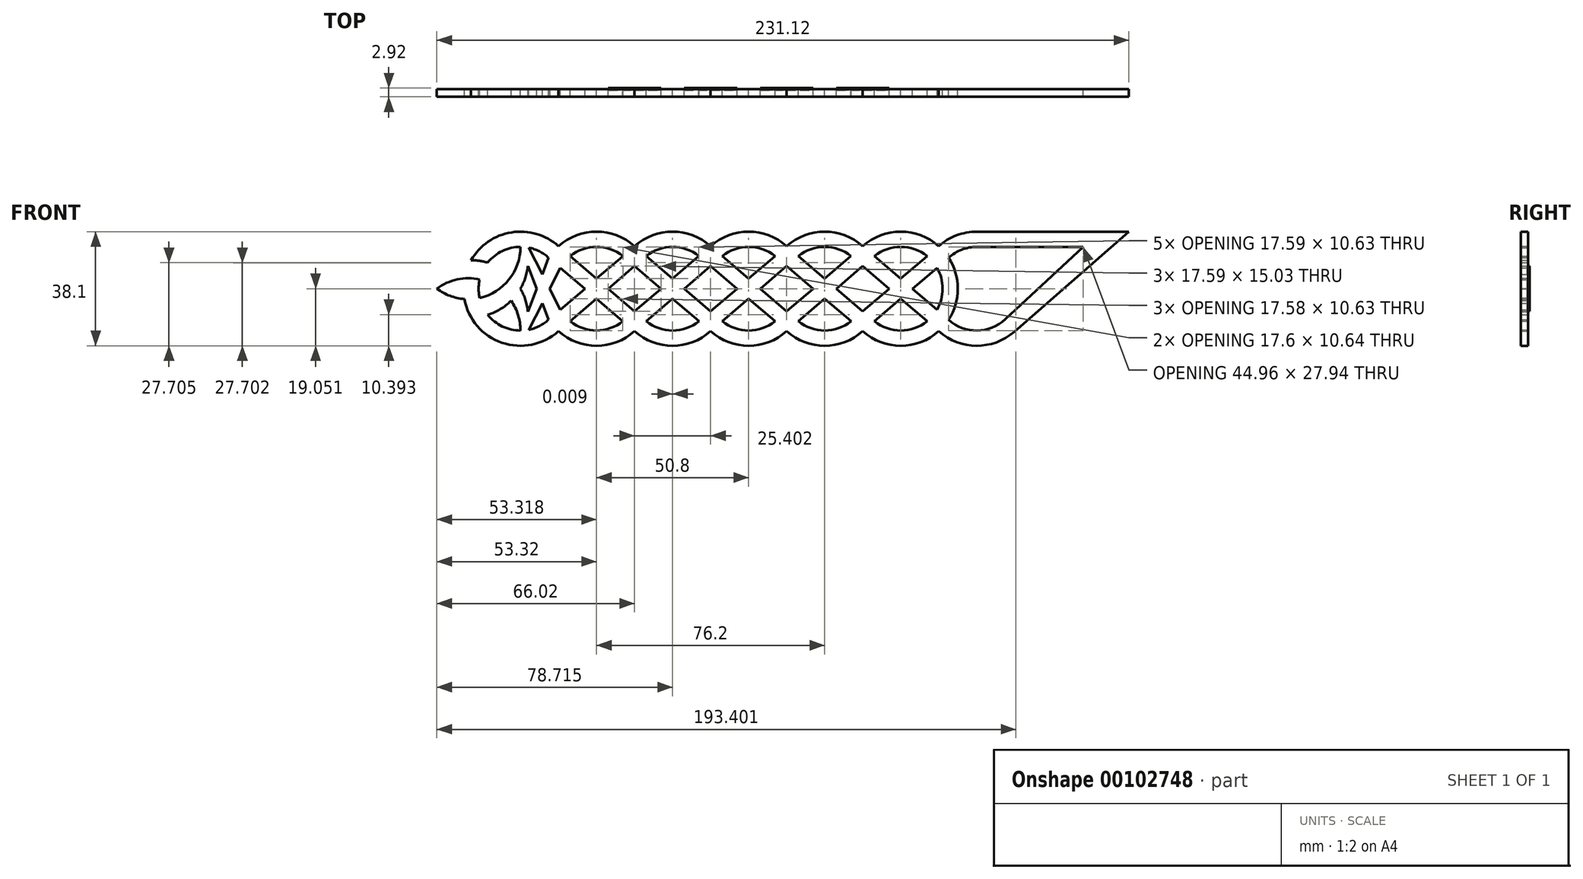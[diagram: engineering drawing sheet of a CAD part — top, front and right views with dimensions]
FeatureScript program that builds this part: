
annotation { "Feature Type Name" : "Feature", "Feature Type Description" : "" }
export const myFeature = defineFeature(function(context is Context, id is Id, definition is map)
    precondition{}
    {
        {
            var Q0;
            Q0=qCreatedBy(makeId("Front.planeOp"),FACE);
            var sketch = newSketch(context, id + "F3", { "sketchPlane" : qUnion([Q0])});
            skPoint(sketch, "E0", {"position": v(0, 0) * mm});
            skLineSegment(sketch, "E1.bottom", {"start": v(0, 0) * mm, "end": v(0, 0) * mm});
            skLineSegment(sketch, "E1.top", {"start": v(0, 0) * mm, "end": v(0, 0) * mm});
            skLineSegment(sketch, "E1.left", {"start": v(0, 0) * mm, "end": v(0, 0) * mm});
            skLineSegment(sketch, "E1.right", {"start": v(0, 0) * mm, "end": v(0, 0) * mm});
            skLineSegment(sketch, "E2.bottom", {"start": v(76.2, 19.05) * mm, "end": v(-76.2, 19.05) * mm, "construction": true});
            skLineSegment(sketch, "E2.top", {"start": v(76.2, -19.05) * mm, "end": v(-76.2, -19.05) * mm, "construction": true});
            skPoint(sketch, "E3", {"position": v(-76.2, 19.05) * mm});
            skPoint(sketch, "E4", {"position": v(76.2, 19.05) * mm});
            skPoint(sketch, "E5", {"position": v(76.2, -19.05) * mm});
            skPoint(sketch, "E6", {"position": v(-76.2, -19.05) * mm});
            skPoint(sketch, "E7", {"position": v(-76.2, 13.97) * mm});
            skPoint(sketch, "E8", {"position": v(-76.2, -13.97) * mm});
            skPoint(sketch, "E9", {"position": v(76.2, -13.97) * mm});
            skPoint(sketch, "E10", {"position": v(-50.8, 19.05) * mm});
            skPoint(sketch, "E11", {"position": v(-25.4, 19.05) * mm});
            skPoint(sketch, "E12", {"position": v(0, 19.05) * mm});
            skPoint(sketch, "E13", {"position": v(25.4, 19.05) * mm});
            skPoint(sketch, "E14", {"position": v(50.8, 19.05) * mm});
            skPoint(sketch, "E15", {"position": v(-50.8, 13.97) * mm});
            skPoint(sketch, "E16", {"position": v(-25.4, 13.97) * mm});
            skPoint(sketch, "E17", {"position": v(0, 13.97) * mm});
            skPoint(sketch, "E18", {"position": v(25.4, 13.97) * mm});
            skPoint(sketch, "E19", {"position": v(50.8, 13.97) * mm});
            skPoint(sketch, "E20", {"position": v(76.2, 13.97) * mm});
            skLineSegment(sketch, "E21", {"start": v(-76.2, 0) * mm, "end": v(-54.7, 0) * mm, "construction": true});
            skPoint(sketch, "E22", {"position": v(-76.2, 0) * mm});
            skPoint(sketch, "E23", {"position": v(76.2, 0) * mm});
            skPoint(sketch, "E24.MirrorP", {"position": v(-50.8, -19.05) * mm});
            skPoint(sketch, "E25.MirrorP", {"position": v(-50.8, -13.97) * mm});
            skPoint(sketch, "E26.MirrorP", {"position": v(-25.4, -19.05) * mm});
            skPoint(sketch, "E27.MirrorP", {"position": v(-25.4, -13.97) * mm});
            skPoint(sketch, "E28.MirrorP", {"position": v(0, -19.05) * mm});
            skPoint(sketch, "E29.MirrorP", {"position": v(0, -13.97) * mm});
            skPoint(sketch, "E30.MirrorP", {"position": v(25.4, -13.97) * mm});
            skPoint(sketch, "E31.MirrorP", {"position": v(25.4, -19.05) * mm});
            skPoint(sketch, "E32.MirrorP", {"position": v(50.8, -13.97) * mm});
            skPoint(sketch, "E33.MirrorP", {"position": v(50.8, -19.05) * mm});
            skPoint(sketch, "E34", {"position": v(-50.8, 0) * mm});
            skPoint(sketch, "E35", {"position": v(-25.4, 0) * mm});
            skPoint(sketch, "E36", {"position": v(25.4, 0) * mm});
            skPoint(sketch, "E37", {"position": v(50.8, 0) * mm});
            skArc(sketch, "E38", {"start": v(-66.8, 10.34) * mm, "mid": v(-70.21, 12.62) * mm, "end": v(-74.14, 13.82) * mm});
            skArc(sketch, "E39", {"start": v(-63.5, -5.82) * mm, "mid": v(-63.2, -6.42) * mm, "end": v(-62.9, -7) * mm, "construction": true});
            skArc(sketch, "E40", {"start": v(-63.75, -13.97) * mm, "mid": v(-50.8, -19.05) * mm, "end": v(-37.85, -13.97) * mm});
            skArc(sketch, "E41", {"start": v(-8.8, -10.86) * mm, "mid": v(0, -13.97) * mm, "end": v(8.8, -10.85) * mm});
            skArc(sketch, "E42", {"start": v(-12.7, -14.2) * mm, "mid": v(0, -19.05) * mm, "end": v(12.7, -14.2) * mm});
            skArc(sketch, "E43", {"start": v(16.6, -10.86) * mm, "mid": v(25.8, -13.96) * mm, "end": v(34.8, -10.34) * mm});
            skArc(sketch, "E44", {"start": v(12.7, -14.2) * mm, "mid": v(25.4, -19.05) * mm, "end": v(38.1, -14.2) * mm});
            skArc(sketch, "E45", {"start": v(42, -10.86) * mm, "mid": v(59.88, -10.62) * mm, "end": v(62.9, 7) * mm});
            skArc(sketch, "E46", {"start": v(38.1, -14.2) * mm, "mid": v(63.18, -14.48) * mm, "end": v(66.8, 10.34) * mm});
            skArc(sketch, "E47", {"start": v(76.2, 13.97) * mm, "mid": v(71.16, 13.03) * mm, "end": v(66.8, 10.34) * mm});
            skArc(sketch, "E48", {"start": v(76.2, 19.05) * mm, "mid": v(69.4, 17.8) * mm, "end": v(63.5, 14.2) * mm});
            skPoint(sketch, "E49", {"position": v(127, 19.05) * mm});
            skLineSegment(sketch, "E50", {"start": v(76.2, 19.05) * mm, "end": v(127, 19.05) * mm});
            skLineSegment(sketch, "E51", {"start": v(127, 19.05) * mm, "end": v(88.73, -14.35) * mm});
            skPoint(sketch, "E52", {"position": v(111.76, 13.97) * mm});
            skLineSegment(sketch, "E53", {"start": v(111.76, 13.97) * mm, "end": v(85.7, -10.23) * mm});
            skLineSegment(sketch, "E54", {"start": v(85.7, -10.23) * mm, "end": v(111.76, 13.97) * mm, "construction": true});
            skLineSegment(sketch, "E55", {"start": v(111.76, 13.97) * mm, "end": v(76.2, 13.97) * mm});
            skPoint(sketch, "E56", {"position": v(-109.2, 0) * mm});
            skPoint(sketch, "E57", {"position": v(-104.12, 0) * mm});
            skPoint(sketch, "E58", {"position": v(-71.12, 18.36) * mm});
            skLineSegment(sketch, "E59.trimOffspring", {"start": v(-63.75, 13.97) * mm, "end": v(-63.25, 13.97) * mm, "construction": true});
            skLineSegment(sketch, "E60", {"start": v(-63.5, -14.2) * mm, "end": v(-50.8, -3.34) * mm});
            skLineSegment(sketch, "E61", {"start": v(-66.8, -10.34) * mm, "end": v(-54.7, 0) * mm});
            skLineSegment(sketch, "E62", {"start": v(-62.9, 7) * mm, "end": v(-42.01, -10.86) * mm});
            skLineSegment(sketch, "E63", {"start": v(-37.78, -14.48) * mm, "end": v(-37.78, -14.48) * mm});
            skLineSegment(sketch, "E64", {"start": v(-38.1, -7.51) * mm, "end": v(-59.6, 10.85) * mm});
            skArc(sketch, "E65.trimOffspring", {"start": v(-63.25, 13.97) * mm, "mid": v(-79.04, 18.84) * mm, "end": v(-92.7, 9.52) * mm});
            skPoint(sketch, "E66.orphan", {"position": v(-71.12, -18.36) * mm});
            skPoint(sketch, "E67.orphan", {"position": v(-63.5, 5.82) * mm});
            skPoint(sketch, "E68.MirrorCS.start.orphan", {"position": v(-63.5, -5.82) * mm});
            skArc(sketch, "E69", {"start": v(-76.2, -13.97) * mm, "mid": v(-77, -8.76) * mm, "end": v(-79.3, -4.03) * mm});
            skArc(sketch, "E70", {"start": v(-76.2, -19.05) * mm, "mid": v(-73.65, -9.52) * mm, "end": v(-76.2, 0) * mm});
            skArc(sketch, "E71.MirrorCS", {"start": v(-76.2, 13.97) * mm, "mid": v(-80.03, 3.06) * mm, "end": v(-89.83, -3.06) * mm});
            skArc(sketch, "E72.MirrorCS", {"start": v(-76.2, 19.05) * mm, "mid": v(-74.97, 2.54) * mm, "end": v(-87.13, -8.7) * mm});
            skLineSegment(sketch, "E73", {"start": v(-76.2, -19.05) * mm, "end": v(-75.31, -17.31) * mm, "construction": true});
            skLineSegment(sketch, "E74", {"start": v(-73.74, -7.62) * mm, "end": v(-70.8, 0) * mm});
            skLineSegment(sketch, "E75", {"start": v(-62.9, -7) * mm, "end": v(-73.47, 13.7) * mm});
            skLineSegment(sketch, "E76", {"start": v(-66.8, -10.34) * mm, "end": v(-73.74, 7.62) * mm});
            skLineSegment(sketch, "E77", {"start": v(-12.45, 14.42) * mm, "end": v(-25.4, 3.34) * mm});
            skLineSegment(sketch, "E78", {"start": v(-41.4, -10.34) * mm, "end": v(-41.4, -10.34) * mm});
            skLineSegment(sketch, "E79", {"start": v(-38.12, -14.22) * mm, "end": v(-25.4, -3.34) * mm});
            skArc(sketch, "E80.trimOffspring", {"start": v(-38.1, 14.2) * mm, "mid": v(-53.34, 18.88) * mm, "end": v(-66.8, 10.34) * mm});
            skArc(sketch, "E81.trimOffspring", {"start": v(-38.1, -14.2) * mm, "mid": v(-25.4, -19.05) * mm, "end": v(-12.7, -14.2) * mm});
            skLineSegment(sketch, "E82", {"start": v(-34.2, 10.85) * mm, "end": v(-12.7, -7.52) * mm});
            skLineSegment(sketch, "E83", {"start": v(12.45, 13.97) * mm, "end": v(0, 3.33) * mm});
            skLineSegment(sketch, "E84", {"start": v(-8.8, 10.85) * mm, "end": v(12.7, -7.52) * mm});
            skLineSegment(sketch, "E85", {"start": v(-12.7, 7.52) * mm, "end": v(8.8, -10.85) * mm});
            skArc(sketch, "E86.trimOffspring", {"start": v(-9.4, 10.34) * mm, "mid": v(-9.4, 10.34) * mm, "end": v(-9.4, 10.34) * mm, "construction": true});
            skArc(sketch, "E87.trimOffspring", {"start": v(-34.2, -10.86) * mm, "mid": v(-25.04, -13.97) * mm, "end": v(-16.05, -10.38) * mm});
            skArc(sketch, "E88.trimOffspring", {"start": v(-16.61, 10.86) * mm, "mid": v(-25.8, 13.96) * mm, "end": v(-34.8, 10.34) * mm});
            skArc(sketch, "E89.trimOffspring", {"start": v(-12.7, 14.2) * mm, "mid": v(-25.57, 19.05) * mm, "end": v(-38.35, 13.97) * mm});
            skLineSegment(sketch, "E90", {"start": v(16, 10.34) * mm, "end": v(3.9, 0) * mm});
            skArc(sketch, "E91.trimOffspring", {"start": v(38.1, 14.2) * mm, "mid": v(25.23, 19.05) * mm, "end": v(12.45, 13.97) * mm});
            skArc(sketch, "E92.trimOffspring", {"start": v(34.19, 10.86) * mm, "mid": v(25, 13.96) * mm, "end": v(16, 10.34) * mm});
            skArc(sketch, "E93.trimOffspring", {"start": v(8.8, 10.85) * mm, "mid": v(-0.4, 13.96) * mm, "end": v(-9.4, 10.34) * mm});
            skArc(sketch, "E94.trimOffspring", {"start": v(12.7, 14.2) * mm, "mid": v(-0.17, 19.05) * mm, "end": v(-12.95, 13.97) * mm});
            skLineSegment(sketch, "E95", {"start": v(8.8, -10.85) * mm, "end": v(21.5, 0) * mm});
            skLineSegment(sketch, "E96", {"start": v(41.4, 10.34) * mm, "end": v(29.31, 0) * mm});
            skLineSegment(sketch, "E97", {"start": v(12.7, 7.52) * mm, "end": v(34.2, -10.85) * mm});
            skLineSegment(sketch, "E98", {"start": v(16.6, 10.86) * mm, "end": v(38.1, -7.51) * mm});
            skLineSegment(sketch, "E99", {"start": v(63.5, 14.2) * mm, "end": v(50.8, 3.34) * mm});
            skLineSegment(sketch, "E100.trimOffspring", {"start": v(63.25, -13.97) * mm, "end": v(63.75, -13.97) * mm, "construction": true});
            skLineSegment(sketch, "E101", {"start": v(66.8, 10.34) * mm, "end": v(54.71, 0) * mm});
            skArc(sketch, "E102.trimOffspring", {"start": v(63.25, -13.97) * mm, "mid": v(75.91, -19.05) * mm, "end": v(88.73, -14.35) * mm});
            skArc(sketch, "E103.trimOffspring", {"start": v(66.8, -10.34) * mm, "mid": v(76.28, -13.97) * mm, "end": v(85.7, -10.23) * mm});
            skLineSegment(sketch, "E104", {"start": v(42, 10.86) * mm, "end": v(62.9, -7) * mm});
            skLineSegment(sketch, "E105", {"start": v(38.1, 7.52) * mm, "end": v(59.6, -10.85) * mm});
            skArc(sketch, "E106.trimOffspring", {"start": v(-74.14, -13.82) * mm, "mid": v(-70.21, -12.62) * mm, "end": v(-66.8, -10.34) * mm});
            skArc(sketch, "E107.trimOffspring", {"start": v(-76.2, 13.97) * mm, "mid": v(-82.27, 12.58) * mm, "end": v(-87.13, 8.7) * mm});
            skArc(sketch, "E108.trimOffspring", {"start": v(-94.94, 3.44) * mm, "mid": v(-85.37, -16.7) * mm, "end": v(-63.25, -13.97) * mm});
            skArc(sketch, "E109.trimOffspring", {"start": v(-89.83, 3.06) * mm, "mid": v(-87.1, -8.73) * mm, "end": v(-76.2, -13.97) * mm});
            skArc(sketch, "E110.trimOffspring", {"start": v(-94.94, -3.44) * mm, "mid": v(-99.77, -2.38) * mm, "end": v(-104.12, 0) * mm});
            skArc(sketch, "E111.trimOffspring", {"start": v(-92.7, -9.53) * mm, "mid": v(-102.22, -6.97) * mm, "end": v(-109.2, 0) * mm});
            skArc(sketch, "E112.trimOffspring", {"start": v(-83.2, 0) * mm, "mid": v(-93.65, 3.48) * mm, "end": v(-104.12, 0) * mm});
            skArc(sketch, "E113.trimOffspring", {"start": v(-79.3, 4.03) * mm, "mid": v(-95.24, 9.35) * mm, "end": v(-109.2, 0) * mm});
            skLineSegment(sketch, "E114.trimOffspring", {"start": v(-68.93, 4.83) * mm, "end": v(-66.8, 10.34) * mm});
            skLineSegment(sketch, "E115.trimOffspring", {"start": v(-66.47, 0) * mm, "end": v(-62.9, 7) * mm});
            skPoint(sketch, "E116.orphan", {"position": v(-66.8, -10.34) * mm});
            skArc(sketch, "E117.trimOffspring", {"start": v(-59.6, -10.86) * mm, "mid": v(-50.4, -13.96) * mm, "end": v(-41.4, -10.34) * mm});
            skLineSegment(sketch, "E118.trimOffspring", {"start": v(-50.8, 3.33) * mm, "end": v(-38.35, 13.97) * mm});
            skLineSegment(sketch, "E119.trimOffspring", {"start": v(-46.9, 0) * mm, "end": v(-34.8, 10.34) * mm});
            skLineSegment(sketch, "E120.trimOffspring", {"start": v(-46.9, 0) * mm, "end": v(-29.3, 0) * mm, "construction": true});
            skLineSegment(sketch, "E121.trimOffspring", {"start": v(-37.85, -13.97) * mm, "end": v(-37.83, -13.97) * mm, "construction": true});
            skLineSegment(sketch, "E122.trimOffspring", {"start": v(-63.75, -13.97) * mm, "end": v(-63.23, -13.97) * mm, "construction": true});
            skLineSegment(sketch, "E123.trimOffspring", {"start": v(-73.47, -13.7) * mm, "end": v(-68.93, -4.83) * mm});
            skLineSegment(sketch, "E124.trimOffspring", {"start": v(-75.31, 17.31) * mm, "end": v(-76.2, 19.05) * mm, "construction": true});
            skLineSegment(sketch, "E125.trimOffspring", {"start": v(-38.1, 7.52) * mm, "end": v(-16.6, -10.85) * mm});
            skArc(sketch, "E126.trimOffspring", {"start": v(-42, 10.85) * mm, "mid": v(-53.34, 13.74) * mm, "end": v(-62.9, 7) * mm});
            skLineSegment(sketch, "E127.trimOffspring", {"start": v(-29.3, 0) * mm, "end": v(-41.4, -10.34) * mm});
            skLineSegment(sketch, "E128.trimOffspring", {"start": v(-21.5, 0) * mm, "end": v(21.5, 0) * mm, "construction": true});
            skLineSegment(sketch, "E129.trimOffspring", {"start": v(-21.5, 0) * mm, "end": v(-9.4, 10.34) * mm});
            skLineSegment(sketch, "E130.trimOffspring", {"start": v(-38.1, -14.2) * mm, "end": v(-37.78, -14.48) * mm, "construction": true});
            skLineSegment(sketch, "E131.trimOffspring", {"start": v(-3.9, 0) * mm, "end": v(-16.6, -10.85) * mm});
            skLineSegment(sketch, "E132.trimOffspring", {"start": v(0, -3.34) * mm, "end": v(-12.7, -14.2) * mm});
            skLineSegment(sketch, "E133.trimOffspring", {"start": v(25.4, 3.34) * mm, "end": v(38.1, 14.2) * mm});
            skLineSegment(sketch, "E134.trimOffspring", {"start": v(29.31, 0) * mm, "end": v(46.9, 0) * mm, "construction": true});
            skLineSegment(sketch, "E135.trimOffspring", {"start": v(25.4, -3.34) * mm, "end": v(12.7, -14.2) * mm});
            skLineSegment(sketch, "E136.trimOffspring", {"start": v(46.9, 0) * mm, "end": v(34.8, -10.34) * mm});
            skLineSegment(sketch, "E137.trimOffspring", {"start": v(50.8, -3.34) * mm, "end": v(38.1, -14.2) * mm});
            skArc(sketch, "E138.trimOffspring", {"start": v(59.6, 10.86) * mm, "mid": v(50.4, 13.96) * mm, "end": v(41.4, 10.34) * mm});
            skArc(sketch, "E139.trimOffspring", {"start": v(63.5, 14.2) * mm, "mid": v(50.8, 19.05) * mm, "end": v(38.1, 14.2) * mm});
            skPoint(sketch, "E140.orphan", {"position": v(-12.45, 13.97) * mm});
            skSolve(sketch);
        }
        {
            var Q0;
            {var subQ6=sQuery(id+"F3.wireOp",EDGE,"E47");Q0=makeQuery(id+"F3.imprint","IMPRINT",FACE,{"disambiguationData":[TD([[makeQuery(id+"F3.imprint","IMPRINT",EDGE,{"derivedFrom":subQ6}),-1.0]])]});}
            var Q1;
            {var subQ0=sQuery(id+"F3.wireOp",EDGE,"E137.trimOffspring");var subQ5=sQuery(id+"F3.wireOp",EDGE,"E45");var subQ9=makeQuery(id+"F3.imprint","INTERSECT",VERTEX,{"derivedFrom":[subQ5,subQ0]});Q1=makeQuery(id+"F3.imprint","IMPRINT",FACE,{"disambiguationData":[TD([[makeQuery(id+"F3.imprint","IMPRINT",EDGE,{"disambiguationData":[TD([[subQ9,-1.0]])],"derivedFrom":subQ5}),-1.0]])]});}
            var Q2;
            {var subQ0=sQuery(id+"F3.wireOp",EDGE,"E104");var subQ9=sQuery(id+"F3.wireOp",EDGE,"E45");var subQ10=makeQuery(id+"F3.imprint","INTERSECT",VERTEX,{"derivedFrom":[subQ9,subQ0]});Q2=makeQuery(id+"F3.imprint","IMPRINT",FACE,{"disambiguationData":[TD([[makeQuery(id+"F3.imprint","IMPRINT",EDGE,{"disambiguationData":[TD([[subQ10,1.0]])],"derivedFrom":subQ9}),1.0]])]});}
            var Q3;
            {var subQ13=sQuery(id+"F3.wireOp",EDGE,"E139.trimOffspring");Q3=makeQuery(id+"F3.imprint","IMPRINT",FACE,{"disambiguationData":[TD([[makeQuery(id+"F3.imprint","IMPRINT",EDGE,{"derivedFrom":subQ13}),1.0]])]});}
            var Q4;
            {var subQ5=sQuery(id+"F3.wireOp",EDGE,"E44");Q4=makeQuery(id+"F3.imprint","IMPRINT",FACE,{"disambiguationData":[TD([[makeQuery(id+"F3.imprint","IMPRINT",EDGE,{"derivedFrom":subQ5}),1.0]])]});}
            var Q5;
            {var subQ4=sQuery(id+"F3.wireOp",EDGE,"E136.trimOffspring");var subQ5=sQuery(id+"F3.wireOp",EDGE,"E43");var subQ6=makeQuery(id+"F3.imprint","INTERSECT",VERTEX,{"derivedFrom":[subQ5,subQ4]});Q5=makeQuery(id+"F3.imprint","IMPRINT",FACE,{"disambiguationData":[TD([[makeQuery(id+"F3.imprint","IMPRINT",EDGE,{"disambiguationData":[TD([[subQ6,1.0]])],"derivedFrom":subQ5}),1.0]])]});}
            var Q6;
            {var subQ1=sQuery(id+"F3.wireOp",EDGE,"E83");var subQ11=sQuery(id+"F3.wireOp",EDGE,"E91.trimOffspring");var subQ13=makeQuery(id+"F3.imprint","INTERSECT",VERTEX,{"derivedFrom":[subQ1,subQ11]});Q6=makeQuery(id+"F3.imprint","IMPRINT",FACE,{"disambiguationData":[TD([[makeQuery(id+"F3.imprint","IMPRINT",EDGE,{"disambiguationData":[TD([[subQ13,-1.0]])],"derivedFrom":subQ1}),1.0]])]});}
            var Q7;
            {var subQ4=sQuery(id+"F3.wireOp",EDGE,"E41");Q7=makeQuery(id+"F3.imprint","IMPRINT",FACE,{"disambiguationData":[TD([[makeQuery(id+"F3.imprint","IMPRINT",EDGE,{"derivedFrom":subQ4}),-1.0]])]});}
            var Q8;
            {var subQ0=sQuery(id+"F3.wireOp",EDGE,"E87.trimOffspring");var subQ1=sQuery(id+"F3.wireOp",EDGE,"E79");var subQ2=makeQuery(id+"F3.imprint","INTERSECT",VERTEX,{"derivedFrom":[subQ1,subQ0]});Q8=makeQuery(id+"F3.imprint","IMPRINT",FACE,{"disambiguationData":[TD([[makeQuery(id+"F3.imprint","IMPRINT",EDGE,{"disambiguationData":[TD([[subQ2,1.0]])],"derivedFrom":subQ1}),-1.0]])]});}
            var Q9;
            {var subQ9=sQuery(id+"F3.wireOp",EDGE,"E77");var subQ17=makeQuery(id+"F3.imprint","INTERSECT",VERTEX,{"derivedFrom":[subQ9,sQuery(id+"F3.wireOp",EDGE,"E88.trimOffspring")]});Q9=makeQuery(id+"F3.imprint","IMPRINT",FACE,{"disambiguationData":[TD([[makeQuery(id+"F3.imprint","IMPRINT",EDGE,{"disambiguationData":[TD([[subQ17,1.0]])],"derivedFrom":subQ9}),1.0]])]});}
            var Q10;
            {var subQ4=sQuery(id+"F3.wireOp",EDGE,"E118.trimOffspring");var subQ5=sQuery(id+"F3.wireOp",EDGE,"E64");var subQ6=makeQuery(id+"F3.imprint","INTERSECT",VERTEX,{"derivedFrom":[subQ5,subQ4]});Q10=makeQuery(id+"F3.imprint","IMPRINT",FACE,{"disambiguationData":[TD([[makeQuery(id+"F3.imprint","IMPRINT",EDGE,{"disambiguationData":[TD([[subQ6,1.0]])],"derivedFrom":subQ5}),-1.0]])]});}
            var Q11;
            {var subQ9=sQuery(id+"F3.wireOp",EDGE,"E79");var subQ13=sQuery(id+"F3.wireOp",EDGE,"E40");var subQ17=makeQuery(id+"F3.imprint","INTERSECT",VERTEX,{"derivedFrom":[subQ13,subQ9]});Q11=makeQuery(id+"F3.imprint","IMPRINT",FACE,{"disambiguationData":[TD([[makeQuery(id+"F3.imprint","IMPRINT",EDGE,{"disambiguationData":[TD([[subQ17,-1.0]])],"derivedFrom":subQ13}),1.0]])]});}
            var Q12;
            {var subQ4=sQuery(id+"F3.wireOp",EDGE,"E62");var subQ5=makeQuery(id+"F3.imprint","INTERSECT",VERTEX,{"derivedFrom":[sQuery(id+"F3.wireOp",EDGE,"E60"),subQ4]});Q12=makeQuery(id+"F3.imprint","IMPRINT",FACE,{"disambiguationData":[TD([[makeQuery(id+"F3.imprint","IMPRINT",EDGE,{"disambiguationData":[TD([[subQ5,1.0]])],"derivedFrom":subQ4}),1.0]])]});}
            var Q13;
            {var subQ0=sQuery(id+"F3.wireOp",EDGE,"E114.trimOffspring");Q13=makeQuery(id+"F3.imprint","IMPRINT",FACE,{"disambiguationData":[TD([[makeQuery(id+"F3.imprint","IMPRINT",EDGE,{"derivedFrom":subQ0}),-1.0]])]});}
            var Q14;
            {var subQ2=sQuery(id+"F3.wireOp",EDGE,"E62");var subQ6=sQuery(id+"F3.wireOp",EDGE,"E60");var subQ7=makeQuery(id+"F3.imprint","INTERSECT",VERTEX,{"derivedFrom":[subQ6,subQ2]});Q14=makeQuery(id+"F3.imprint","IMPRINT",FACE,{"disambiguationData":[TD([[makeQuery(id+"F3.imprint","IMPRINT",EDGE,{"disambiguationData":[TD([[subQ7,1.0]])],"derivedFrom":subQ6}),1.0]])]});}
            var Q15;
            {var subQ4=sQuery(id+"F3.wireOp",EDGE,"E72.MirrorCS");var subQ5=sQuery(id+"F3.wireOp",EDGE,"E38");var subQ6=makeQuery(id+"F3.imprint","INTERSECT",VERTEX,{"derivedFrom":[subQ5,subQ4]});Q15=makeQuery(id+"F3.imprint","IMPRINT",FACE,{"disambiguationData":[TD([[makeQuery(id+"F3.imprint","IMPRINT",EDGE,{"disambiguationData":[TD([[subQ6,1.0]])],"derivedFrom":subQ5}),1.0]])]});}
            var Q16;
            {var subQ0=sQuery(id+"F3.wireOp",EDGE,"E74");Q16=makeQuery(id+"F3.imprint","IMPRINT",FACE,{"disambiguationData":[TD([[makeQuery(id+"F3.imprint","IMPRINT",EDGE,{"derivedFrom":subQ0}),-1.0]])]});}
            var Q17;
            {var subQ0=sQuery(id+"F3.wireOp",EDGE,"E72.MirrorCS");var subQ1=sQuery(id+"F3.wireOp",EDGE,"E38");var subQ2=makeQuery(id+"F3.imprint","INTERSECT",VERTEX,{"derivedFrom":[subQ1,subQ0]});Q17=makeQuery(id+"F3.imprint","IMPRINT",FACE,{"disambiguationData":[TD([[makeQuery(id+"F3.imprint","IMPRINT",EDGE,{"disambiguationData":[TD([[subQ2,1.0]])],"derivedFrom":subQ1}),-1.0]])]});}
            var Q18;
            {var subQ0=sQuery(id+"F3.wireOp",EDGE,"E107.trimOffspring");Q18=makeQuery(id+"F3.imprint","IMPRINT",FACE,{"disambiguationData":[TD([[makeQuery(id+"F3.imprint","IMPRINT",EDGE,{"derivedFrom":subQ0}),-1.0]])]});}
            var Q19;
            {var subQ10=sQuery(id+"F3.wireOp",EDGE,"E69");Q19=makeQuery(id+"F3.imprint","IMPRINT",FACE,{"disambiguationData":[TD([[makeQuery(id+"F3.imprint","IMPRINT",EDGE,{"derivedFrom":subQ10}),-1.0]])]});}
            var Q20;
            {var subQ1=sQuery(id+"F3.wireOp",EDGE,"E110.trimOffspring");Q20=makeQuery(id+"F3.imprint","IMPRINT",FACE,{"disambiguationData":[TD([[makeQuery(id+"F3.imprint","IMPRINT",EDGE,{"derivedFrom":subQ1}),1.0]])]});}
            extrude(context, id + "F0", {"entities" : qUnion([Q0, Q1, Q2, Q3, Q4, Q5, Q6, Q7, Q8, Q9, Q10, Q11, Q12, Q13, Q14, Q15, Q16, Q17, Q18, Q19, Q20]), "depth" : 2.54 * mm});
        }
        {
            var Q0;
            {var subQ1=sQuery(id+"F3.wireOp",EDGE,"E82");var subQ11=makeQuery(id+"F3.imprint","INTERSECT",VERTEX,{"derivedFrom":[sQuery(id+"F3.wireOp",EDGE,"E77"),subQ1]});Q0=makeQuery(id+"F3.imprint","IMPRINT",FACE,{"disambiguationData":[TD([[makeQuery(id+"F3.imprint","IMPRINT",EDGE,{"disambiguationData":[TD([[subQ11,1.0]])],"derivedFrom":subQ1}),-1.0]])]});}
            extrude(context, id + "F1", {"entities" : qUnion([Q0]), "operationType" : NewBodyOperationType.ADD, "depth" : 2.54 * mm});
        }
        {
            var Q0;
            {var subQ0=sQuery(id+"F3.wireOp",EDGE,"E98");var subQ1=sQuery(id+"F3.wireOp",EDGE,"E96");var subQ2=makeQuery(id+"F3.imprint","INTERSECT",VERTEX,{"derivedFrom":[subQ1,subQ0]});Q0=makeQuery(id+"F3.imprint","IMPRINT",FACE,{"disambiguationData":[TD([[makeQuery(id+"F3.imprint","IMPRINT",EDGE,{"disambiguationData":[TD([[subQ2,1.0]])],"derivedFrom":subQ1}),1.0]])]});}
            var Q1;
            {var subQ0=sQuery(id+"F3.wireOp",EDGE,"E127.trimOffspring");var subQ1=sQuery(id+"F3.wireOp",EDGE,"E64");var subQ2=makeQuery(id+"F3.imprint","INTERSECT",VERTEX,{"derivedFrom":[subQ1,subQ0]});Q1=makeQuery(id+"F3.imprint","IMPRINT",FACE,{"disambiguationData":[TD([[makeQuery(id+"F3.imprint","IMPRINT",EDGE,{"disambiguationData":[TD([[subQ2,-1.0]])],"derivedFrom":subQ1}),-1.0]])]});}
            var Q2;
            {var subQ0=sQuery(id+"F3.wireOp",EDGE,"E95");var subQ1=sQuery(id+"F3.wireOp",EDGE,"E84");var subQ2=makeQuery(id+"F3.imprint","INTERSECT",VERTEX,{"derivedFrom":[subQ1,subQ0]});Q2=makeQuery(id+"F3.imprint","IMPRINT",FACE,{"disambiguationData":[TD([[makeQuery(id+"F3.imprint","IMPRINT",EDGE,{"disambiguationData":[TD([[subQ2,1.0]])],"derivedFrom":subQ1}),1.0]])]});}
            var Q3;
            {var subQ0=sQuery(id+"F3.wireOp",EDGE,"E131.trimOffspring");var subQ1=sQuery(id+"F3.wireOp",EDGE,"E82");var subQ2=makeQuery(id+"F3.imprint","INTERSECT",VERTEX,{"derivedFrom":[subQ1,subQ0]});Q3=makeQuery(id+"F3.imprint","IMPRINT",FACE,{"disambiguationData":[TD([[makeQuery(id+"F3.imprint","IMPRINT",EDGE,{"disambiguationData":[TD([[subQ2,1.0]])],"derivedFrom":subQ1}),1.0]])]});}
            extrude(context, id + "F2", {"entities" : qUnion([Q0, Q1, Q2, Q3]), "operationType" : NewBodyOperationType.ADD, "endBound" : BoundingType.SYMMETRIC, "oppositeDirection" : true, "depth" : 0.76 * mm, "hasDraft" : true, "draftAngle" : 3 * degree});
        }
    });
